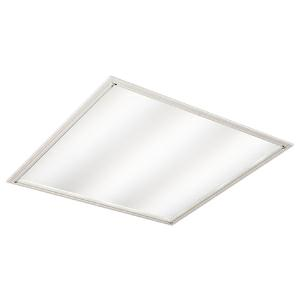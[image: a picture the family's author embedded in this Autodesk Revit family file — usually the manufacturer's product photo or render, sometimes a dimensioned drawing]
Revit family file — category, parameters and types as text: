
# Revit family: 3f_filippi_-_l_320_lgs_3f_filippi_-_22710_-_l_324x10w-940_led_dali_lgs_596x596
name_source: partatom
category: Lighting Fixtures
units: mm (PartAtom-declared; Revit-internal decimal feet)

## family parameters
Cut with Voids When Loaded = No
Host = Face
Light Source = No
Part Type = Normal
Room Calculation Point = No
Round Connector Dimension = Use Diameter
Shared = No

## types (1)
- 3F Filippi - L 320 LGS (1 x LED, 3327 lm, 45 W, 4000 K)
    Apparent Load = 45 VA
    Approval mark = ENEC
    CIE Flux Codes = 62 88 97 100 100
    Color Rendering = 90
    Color Temperature = 4000 K
    Control Gear = Electronic transformer
    Default Elevation = 1800 mm
    Description = ILLUMINOTECHNICAL
Luminous efficiency 100% (DLOR 100%, ULOR 0%).
Initial luminous flux of the luminaire 3327 lm.
Direct symmetric distribution.
Installation Interdistance Transv.D = 1.16 x hu - Long.D = 1.16 x hu.
Average luminance <3000 cd/m² for radial angles >65°.
Tabular UGR (CIE 117 - 4H-8H; S=0.25H; 70/50/20): RUG 17.9 - 17.9.
Beam angle: 85° - 84°.
Luminous efficacy 74 lm/W.
Lifetime (L93/B10): 30000 h. (tq+25°C)
Lifetime (L90/B10): 50000 h. (tq+25°C)
Lifetime (L85/B10): 80000 h. (tq+25°C)
Lifetime (L80/B10): 100000 h. (tq+25°C)
Sudden decreased luminous flux after 50000 hours: 0% (C0).
Photobiological safety in compliance with IEC/TR 62778: RG0 risk exempt, (IEC 62471).
In compliance with IEC/EN 62722-2-1 - IEC/EN 62717 standards.

SOURCE
4 linear LED modules 10W/940.
Energy efficiency class (UE 2019/2020 - UE 2019/2015): E.
CIE 13.3 Colour rendering index: CRI >90 (R9 >50%).
IES TM-30 Fidelity Index: Rf = 92 Rg = 101.
CCT nominal colour temperature 4000 K.
Colour initial tolerance (MacAdam): SDCM 2.

MECHANICAL
Housing in hot-galvanised steel, painted in white polyester.
Micro-prismatic flat diffuser in transparent methacrylate (PMMA), multilenticular exterior, anti-glare, locked to the white painted aluminium perimetral frame, sealing gasket, hinged opening.
Anti-glare opal polycarbonate filter for brightness uniformity.
Luminaire with limited surface temperature. - D - (EN 60598-2-24)
Dimensions: 596x596 mm, height 80 mm. Weight 4.265 kg.
IP54 protection degree for exposed part, IP20 for recessed part.
Mechanical strength to impacts IK06 (1 joule).
Glow-wire test resistance 650°C.

ELECTRICAL
Halogen Free DALI-2 DATI (Parts 251, 252, 253), PUSH-DIM, electronic wiring 230V-50/60Hz, power factor 0.95 at full load, THD <25%, constant output current, SELV, class I, 1 driver, 1 DALI addresse.
Power of the luminaire 45 W.
CE - IEC 60598-1 - EN 60598-1.
SAFE FLICKER: PstLM=<1 and SVM=<0.4 (IEC TR 61547-1 and IEC TR 63158), to ensure a more comfortable and safe light.
Luminaire compliant with EN 60598-2-22 for power supply from a centralised emergency system CPSS (Central Power Supply System), not incorporated in the luminaire - high risk areas excluded. The default power and flux are 100% in AC and 15% in DC.
Ambient temperature from 0°C to +25°C.
Temperature class T6 max 85°C.
Relative humidity UR: <85%.

INSTALLATION
Lay-in recessed fitting.
On request: pull-up recessed fitting with brackets.
False ceiling carving: 580x580 mm.
All accessories dedicated to this product are available on the Catalog and on our website www.3F-Filippi.com.

APPLICATIONS
Environments: sterilized, aseptic.
In environments with VDU's, managerial offices and staterooms, environments involving accurate visual tasks where a diffused and soft light for an optimum visual comfort and the source total shielding are required.

LIGHT MANAGEMENT
Recommended minimum setting: 10%.
The luminaire, equipped with (DALI-2 DATI) driver, can be controlled manually with 3F Easy Dim technology or automatically/manually with wired or wireless DALI/D2D control systems.
The D2D driver guarantees interoperability with other devices with the same certification by making the following information available:
Device Data (Part 251), Energy Report (Part 252), Diagnosis & Maintenance (Part 253).
In electrical systems without a regulation system (manual or automatic) and DALI bus, a suitable jumper must be made on the DA-DA terminals of the appliance.

WARNING
Luminaire designed for disposal/recycling at end-of-life.
Replaceable (LED only) light source by a professional. Replaceable control gear by a professional.
    Height = 0 mm  [stored 0 ft]
    Lamp = 1 x LED
    Lamp Light Flux = 3327 lm
    Lamp Power = 45 W
    Lamp count = 1
    Length = 596 mm
    Lifetime = 50000 h
    Luminous efficacy = 74 lm/W
    Manufacturer = 3F Filippi
    ModVariant = No
    Model = 3F Filippi - 22710 - L 324x10W-940 LED DALI LGS 596x596
    Mounting Place = Ceiling
    Mounting Type = Recessed
    Number of Poles = 1
    OnlyDefault = Yes
    Power Factor = 1
    Product Name = 3F Filippi - L 320 LGS
    Product group = recessed luminaire
    ProductGroupID = 4
    Protection Class = Protection class I
    Protection Degree = IP 20
    RLX_Detail_Level = 1
    RLX_Emergency_Light_Flux = 0 lm
    RLX_Emergency_Type = 0
    RLX_Emergency_Type_DB = No
    RlxData = <blob elided: 36465 chars, md5=37d3cfff>
    Socket = socket
    Standby Power = 0 W
    System Light Flux = 3327 lm
    System Power = 45 W
    Type Comments = Product without accessories
    Type Image = 3ffilippi_l_320_led_lgs.jpg
    URL = http://relux.com
    VarID = ---
    Voltage = 0 V
    Weight = 0.00 kg
    Width = 596 mm

note: [stored X ft] marks values corroborated as IEEE doubles in the binary element streams (Revit-internal decimal feet)

## geometry (parser evidence)
native form markers: Blend x4, Sweep x11
no freeform markers — native parametric forms only
